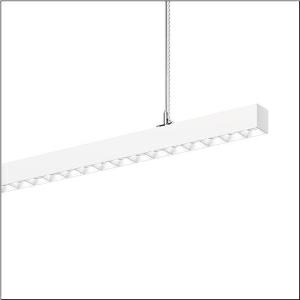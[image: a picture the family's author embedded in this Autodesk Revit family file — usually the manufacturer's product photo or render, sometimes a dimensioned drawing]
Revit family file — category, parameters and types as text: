
# Revit family: silica_r__21_51mx36da47wb_ab97
name_source: partatom
category: Lighting Fixtures
units: mm (PartAtom-declared; Revit-internal decimal feet)

## family parameters
Cut with Voids When Loaded = No
Host = Face
Light Source = No
Part Type = Normal
Room Calculation Point = No
Round Connector Dimension = Use Diameter
Shared = No

## types (1)
- --- (1 x LED, 7060 lm, 40.3 W, 4000K)
    Apparent Load = 40 VA
    CIE Flux Codes = 83 98 100 61 100
    Color Rendering = 80
    Color Temperature = 4000K
    Default Elevation = 1800 mm
    Description = Silica® 21, office luminaire, primary light control with darklight reflector, of PMMA, white, CAT 2 (L<= 3000cd/m²), light emission: direct/indirect distribution, primary light characteristic: symmetric, installation type: suspended mounting, LED, rated luminous flux: 7.060lm, luminous efficacy: 175lm/W, light colour: 840, colour temperature: 4000K, with terminal, 3+2-pole, max. 2.5mm², mains connection: 220..240V, AC, 50/60Hz, rated input power: 40.3W, luminaire housing, of aluminium, traffic white (RAL 9016), length: 1.204mm, width: 53mm, height: 53mm, protection rating (complete): IP20, insulation class (complete): insulation class I (protective earthing), certification: CE, permissible operating ambient temperature: 0..+35°C, standard: EN 50419, packaging unit: 1 piece
    Height = 53 mm
    Lamp = 1 x LED
    Lamp Light Flux = 7060 lm
    Lamp Power = 40.3 W
    Lamp count = 1
    Length = 1204 mm
    Luminous efficacy = 175 lm/W
    Manufacturer = Siteco
    ModVariant = No
    Model = 51MX36DA47WB
    Mounting Place = Ceiling
    Mounting Type = Pendant
    Number of Poles = 1
    OnlyDefault = Yes
    Power Factor = 1
    Product Name = Silica® 21
    Product group = office luminaire | ceiling pendant
    ProductGroupID = 902
    Protection Class = Protection class I
    Protection Degree = IP 20
    RLX_Detail_Level = 1
    RLX_Emergency_Light_Flux = 0 lm
    RLX_Emergency_Type = 0
    RLX_Emergency_Type_DB = No
    RlxData = <blob elided: 40789 chars, md5=b89118a8>
    Socket = socket
    Standby Power = 0 W
    System Light Flux = 7060 lm
    System Power = 40 W
    Type Comments = factory setting: luminous flux: 100 % | dim-lin: 254 | 336 mA
    Type Image = l_1313634.jpg
    URL = http://relux.com
    VarID = @adj_070249
    Voltage = 0 V
    Weight = 0.00 kg
    Width = 53 mm

## geometry (parser evidence)
native form markers: Blend x4, Sweep x12
no freeform markers — native parametric forms only
